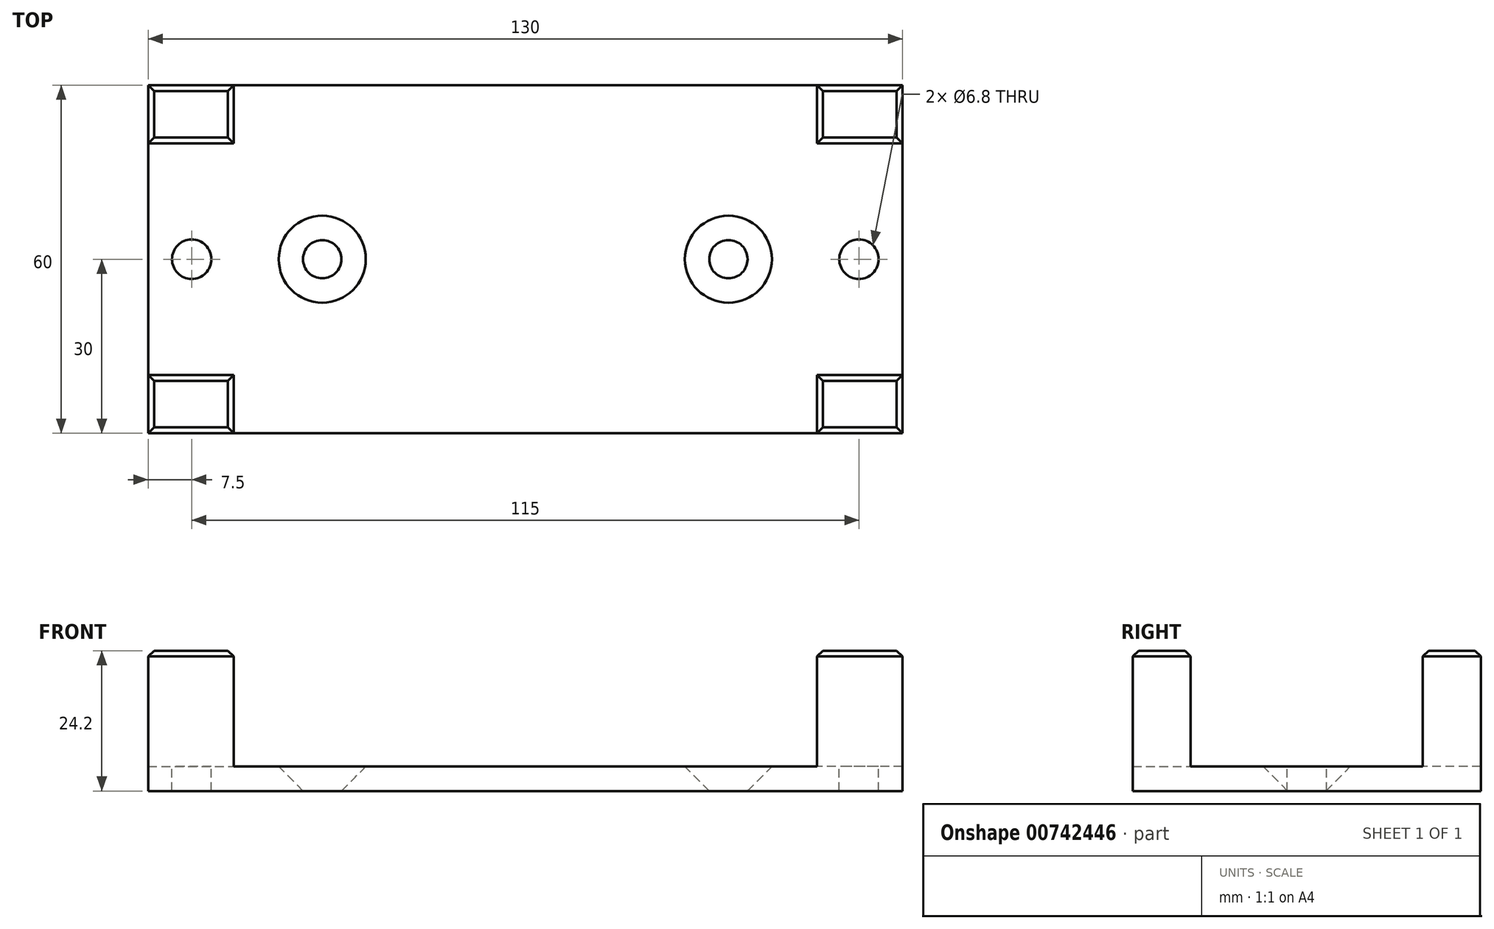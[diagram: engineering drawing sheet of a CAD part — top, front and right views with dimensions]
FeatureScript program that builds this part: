
annotation { "Feature Type Name" : "Feature", "Feature Type Description" : "" }
export const myFeature = defineFeature(function(context is Context, id is Id, definition is map)
    precondition{}
    {
        {
            var Q0;
            Q0=qCreatedBy(makeId("Top.planeOp"),FACE);
            var sketch = newSketch(context, id + "F0", { "sketchPlane" : qUnion([Q0])});
            skLineSegment(sketch, "E0.bottom", {"start": v(65, -30) * mm, "end": v(-65, -30) * mm});
            skLineSegment(sketch, "E0.top", {"start": v(65, 30) * mm, "end": v(-65, 30) * mm});
            skLineSegment(sketch, "E0.left", {"start": v(65, -30) * mm, "end": v(65, 30) * mm});
            skLineSegment(sketch, "E0.right", {"start": v(-65, -30) * mm, "end": v(-65, 30) * mm});
            skPoint(sketch, "E0.middle", {"position": v(0, 0) * mm});
            skSolve(sketch);
        }
        {
            var Q0;
            Q0=makeQuery(id+"F0.imprint","IMPRINT",FACE,{"disambiguationData":[TD([[makeQuery(id+"F0.imprint","IMPRINT",EDGE,{"derivedFrom":sQuery(id+"F0.wireOp",EDGE,"E0.bottom")}),-1.0]])]});
            extrude(context, id + "F1", {"entities" : qUnion([Q0]), "depth" : 4.2 * mm, "offsetDistance" : 25 * mm});
        }
        {
            var Q0;
            Q0=makeQuery(id+"F1.opExtrude","CAP_FACE",FACE,{"disambiguationData":[OSD([sQuery(id+"F0.wireOp",EDGE,"E0.bottom"),sQuery(id+"F0.wireOp",EDGE,"E0.top"),sQuery(id+"F0.wireOp",EDGE,"E0.left"),sQuery(id+"F0.wireOp",EDGE,"E0.right")])],"isStart":false});
            var sketch = newSketch(context, id + "F2", { "sketchPlane" : qUnion([Q0])});
            skLineSegment(sketch, "E1.bottom", {"start": v(-65, 30) * mm, "end": v(-50.25, 30) * mm});
            skLineSegment(sketch, "E1.top", {"start": v(-65, 20) * mm, "end": v(-50.25, 20) * mm});
            skLineSegment(sketch, "E1.left", {"start": v(-65, 30) * mm, "end": v(-65, 20) * mm});
            skLineSegment(sketch, "E1.right", {"start": v(-50.25, 30) * mm, "end": v(-50.25, 20) * mm});
            skLineSegment(sketch, "E2.bottom", {"start": v(65, 30) * mm, "end": v(50.25, 30) * mm});
            skLineSegment(sketch, "E2.top", {"start": v(65, 20) * mm, "end": v(50.25, 20) * mm});
            skLineSegment(sketch, "E2.left", {"start": v(65, 30) * mm, "end": v(65, 20) * mm});
            skLineSegment(sketch, "E2.right", {"start": v(50.25, 30) * mm, "end": v(50.25, 20) * mm});
            skLineSegment(sketch, "E3.bottom", {"start": v(65, -30) * mm, "end": v(50.25, -30) * mm});
            skLineSegment(sketch, "E3.top", {"start": v(65, -20) * mm, "end": v(50.25, -20) * mm});
            skLineSegment(sketch, "E3.left", {"start": v(65, -30) * mm, "end": v(65, -20) * mm});
            skLineSegment(sketch, "E3.right", {"start": v(50.25, -30) * mm, "end": v(50.25, -20) * mm});
            skLineSegment(sketch, "E4.bottom", {"start": v(-65, -30) * mm, "end": v(-50.25, -30) * mm});
            skLineSegment(sketch, "E4.top", {"start": v(-65, -20) * mm, "end": v(-50.25, -20) * mm});
            skLineSegment(sketch, "E4.left", {"start": v(-65, -30) * mm, "end": v(-65, -20) * mm});
            skLineSegment(sketch, "E4.right", {"start": v(-50.25, -30) * mm, "end": v(-50.25, -20) * mm});
            skSolve(sketch);
        }
        {
            var Q0;
            Q0=makeQuery(id+"F2.imprint","IMPRINT",FACE,{"disambiguationData":[TD([[makeQuery(id+"F2.imprint","IMPRINT",EDGE,{"derivedFrom":sQuery(id+"F2.wireOp",EDGE,"E1.bottom")}),1.0]])]});
            var Q1;
            Q1=makeQuery(id+"F2.imprint","IMPRINT",FACE,{"disambiguationData":[TD([[makeQuery(id+"F2.imprint","IMPRINT",EDGE,{"derivedFrom":sQuery(id+"F2.wireOp",EDGE,"E4.bottom")}),-1.0]])]});
            var Q2;
            Q2=makeQuery(id+"F2.imprint","IMPRINT",FACE,{"disambiguationData":[TD([[makeQuery(id+"F2.imprint","IMPRINT",EDGE,{"derivedFrom":sQuery(id+"F2.wireOp",EDGE,"E3.bottom")}),-1.0]])]});
            var Q3;
            Q3=makeQuery(id+"F2.imprint","IMPRINT",FACE,{"disambiguationData":[TD([[makeQuery(id+"F2.imprint","IMPRINT",EDGE,{"derivedFrom":sQuery(id+"F2.wireOp",EDGE,"E2.bottom")}),1.0]])]});
            extrude(context, id + "F3", {"entities" : qUnion([Q0, Q1, Q2, Q3]), "operationType" : NewBodyOperationType.ADD, "depth" : 20 * mm, "offsetDistance" : 25 * mm});
        }
        {
            var Q0;
            Q0=makeQuery(id+"F1.opExtrude","CAP_FACE",FACE,{"disambiguationData":[OSD([sQuery(id+"F0.wireOp",EDGE,"E0.bottom"),sQuery(id+"F0.wireOp",EDGE,"E0.top"),sQuery(id+"F0.wireOp",EDGE,"E0.left"),sQuery(id+"F0.wireOp",EDGE,"E0.right")])],"isStart":false});
            var sketch = newSketch(context, id + "F4", { "sketchPlane" : qUnion([Q0])});
            skPoint(sketch, "E5", {"position": v(57.5, 0) * mm});
            skPoint(sketch, "E5.positionSnap0", {"position": v(65, 0) * mm});
            skPoint(sketch, "E6", {"position": v(-57.5, 0) * mm});
            skSolve(sketch);
        }
        {
            var Q0;
            Q0=sQuery(id+"F4.wireOp",VERTEX,"E5");
            var Q1;
            Q1=sQuery(id+"F4.wireOp",VERTEX,"E6");
            var Q2;
            Q2=makeQuery(id+"F1.opExtrude","SWEPT_BODY",BODY,{"disambiguationData":[OSD([sQuery(id+"F0.wireOp",EDGE,"E0.bottom"),sQuery(id+"F0.wireOp",EDGE,"E0.top"),sQuery(id+"F0.wireOp",EDGE,"E0.left"),sQuery(id+"F0.wireOp",EDGE,"E0.right")])]});
            hole(context, id + "F5", {"style" : HoleStyle.SIMPLE, "endStyle" : HoleEndStyle.THROUGH, "standardTappedOrClearance" : lookupTablePath({ "standard" : "ISO", "engagement" : "75%", "pitch" : "1.25 mm", "size" : "M8", "type" : "Tapped" }), "standardBlindInLast" : lookupTablePath({ "standard" : "ISO", "engagement" : "75%", "pitch" : "1.25 mm", "size" : "M8", "type" : "Tapped" }), "holeDiameter" : 6.8 * mm, "majorDiameter" : 8 * mm, "showTappedDepth" : true, "isTappedThrough" : true, "tappedDepth" : 30 * mm, "tapClearance" : 0, "startFromSketch" : true, "locations" : qUnion([Q0, Q1]), "scope" : qUnion([Q2])});
        }
        {
            var Q0;
            Q0=makeQuery(id+"F1.opExtrude","CAP_FACE",FACE,{"disambiguationData":[OSD([sQuery(id+"F0.wireOp",EDGE,"E0.bottom"),sQuery(id+"F0.wireOp",EDGE,"E0.top"),sQuery(id+"F0.wireOp",EDGE,"E0.left"),sQuery(id+"F0.wireOp",EDGE,"E0.right")])],"isStart":false});
            var sketch = newSketch(context, id + "F6", { "sketchPlane" : qUnion([Q0])});
            skPoint(sketch, "E7", {"position": v(35, 0) * mm});
            skPoint(sketch, "E7.positionSnap0", {"position": v(65, 0) * mm});
            skPoint(sketch, "E8", {"position": v(-35, 0) * mm});
            skSolve(sketch);
        }
        {
            var Q0;
            Q0=sQuery(id+"F6.wireOp",VERTEX,"E7");
            var Q1;
            Q1=sQuery(id+"F6.wireOp",VERTEX,"E8");
            var Q2;
            Q2=makeQuery(id+"F1.opExtrude","SWEPT_BODY",BODY,{"disambiguationData":[OSD([sQuery(id+"F0.wireOp",EDGE,"E0.bottom"),sQuery(id+"F0.wireOp",EDGE,"E0.top"),sQuery(id+"F0.wireOp",EDGE,"E0.left"),sQuery(id+"F0.wireOp",EDGE,"E0.right")])]});
            hole(context, id + "F7", {"style" : HoleStyle.C_SINK, "endStyle" : HoleEndStyle.THROUGH, "standardTappedOrClearance" : lookupTablePath({ "standard" : "ISO", "size" : "6", "type" : "Drilled" }), "standardBlindInLast" : lookupTablePath({ "standard" : "ISO", "size" : "6", "type" : "Drilled" }), "holeDiameter" : 6 * mm, "cSinkDiameter" : 15 * mm, "cSinkAngle" : 90 * degree, "majorDiameter" : 8 * mm, "isTappedThrough" : true, "tappedDepth" : 30 * mm, "tapClearance" : 0, "startFromSketch" : true, "locations" : qUnion([Q0, Q1]), "scope" : qUnion([Q2])});
        }
        {
            var Q0;
            Q0=makeQuery(id+"F3.opExtrude","CAP_EDGE",EDGE,{"disambiguationData":[OSD([sQuery(id+"F2.wireOp",EDGE,"E4.right")])],"isStart":false});
            var Q1;
            Q1=makeQuery(id+"F3.opExtrude","CAP_EDGE",EDGE,{"disambiguationData":[OSD([sQuery(id+"F2.wireOp",EDGE,"E4.bottom")])],"isStart":false});
            var Q2;
            Q2=makeQuery(id+"F3.opExtrude","CAP_EDGE",EDGE,{"disambiguationData":[OSD([sQuery(id+"F2.wireOp",EDGE,"E4.left")])],"isStart":false});
            var Q3;
            Q3=makeQuery(id+"F3.opExtrude","CAP_EDGE",EDGE,{"disambiguationData":[OSD([sQuery(id+"F2.wireOp",EDGE,"E4.top")])],"isStart":false});
            var Q4;
            Q4=makeQuery(id+"F3.opExtrude","CAP_FACE",FACE,{"disambiguationData":[OSD([sQuery(id+"F2.wireOp",EDGE,"E1.bottom"),sQuery(id+"F2.wireOp",EDGE,"E1.top"),sQuery(id+"F2.wireOp",EDGE,"E1.left"),sQuery(id+"F2.wireOp",EDGE,"E1.right")])],"isStart":false});
            var Q5;
            Q5=makeQuery(id+"F3.opExtrude","CAP_FACE",FACE,{"disambiguationData":[OSD([sQuery(id+"F2.wireOp",EDGE,"E3.bottom"),sQuery(id+"F2.wireOp",EDGE,"E3.top"),sQuery(id+"F2.wireOp",EDGE,"E3.left"),sQuery(id+"F2.wireOp",EDGE,"E3.right")])],"isStart":false});
            var Q6;
            Q6=makeQuery(id+"F3.opExtrude","CAP_FACE",FACE,{"disambiguationData":[OSD([sQuery(id+"F2.wireOp",EDGE,"E2.bottom"),sQuery(id+"F2.wireOp",EDGE,"E2.top"),sQuery(id+"F2.wireOp",EDGE,"E2.left"),sQuery(id+"F2.wireOp",EDGE,"E2.right")])],"isStart":false});
            chamfer(context, id + "F8", {"entities" : qUnion([Q0, Q1, Q2, Q3, Q4, Q5, Q6]), "width" : 1 * mm, "tangentPropagation" : true});
        }
    });
